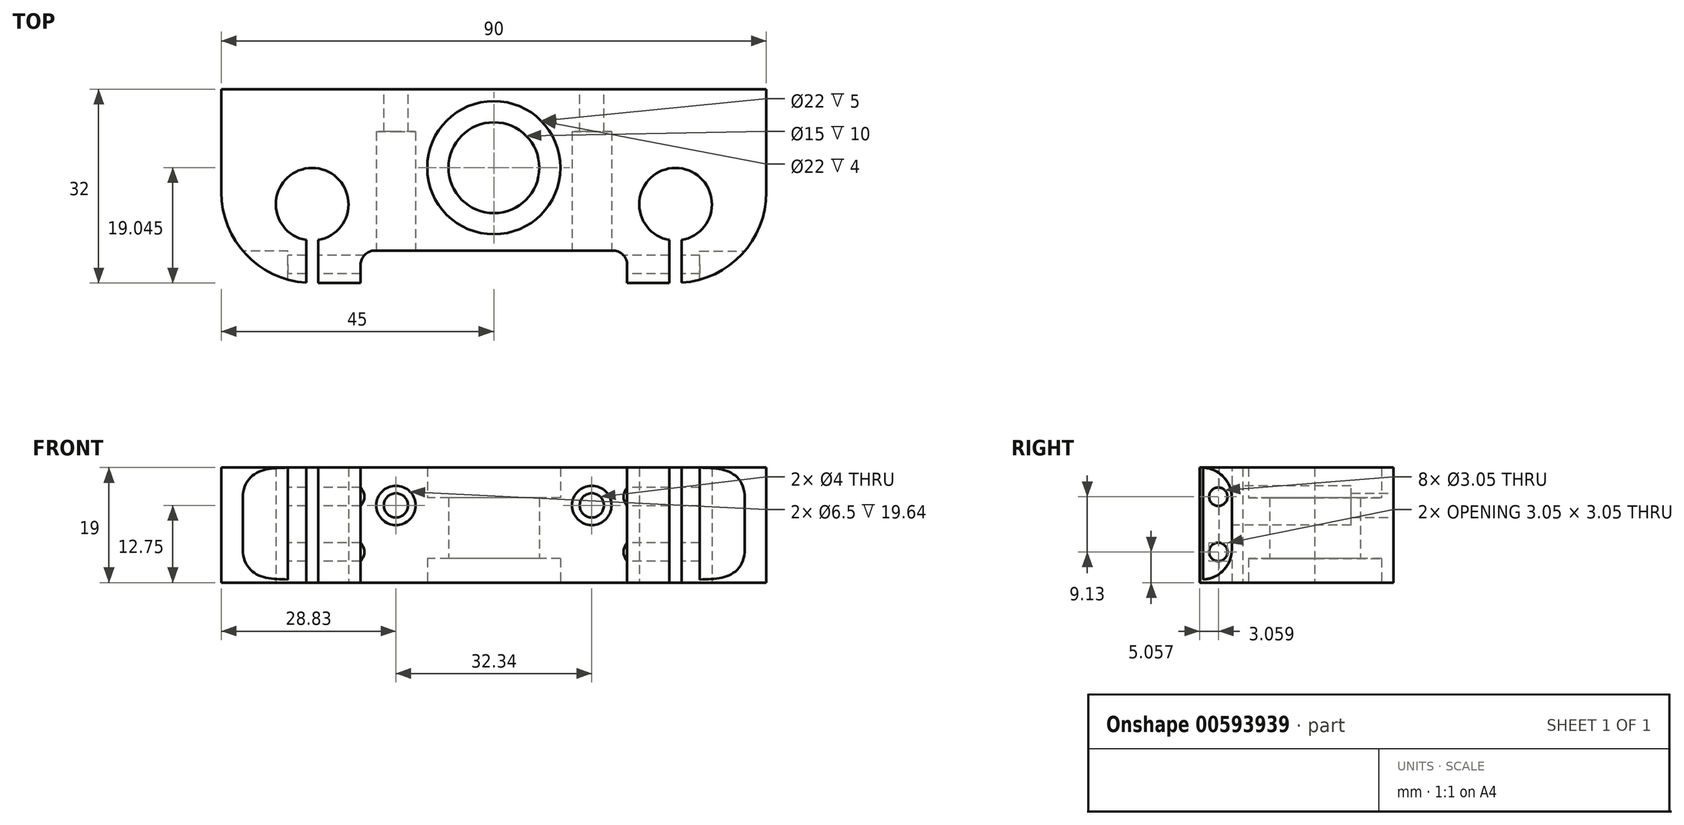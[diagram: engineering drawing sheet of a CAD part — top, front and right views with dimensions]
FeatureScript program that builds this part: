
annotation { "Feature Type Name" : "Feature", "Feature Type Description" : "" }
export const myFeature = defineFeature(function(context is Context, id is Id, definition is map)
    precondition{}
    {
        {
            var Q0;
            Q0=qCreatedBy(makeId("Top.planeOp"),FACE);
            var sketch = newSketch(context, id + "F0", { "sketchPlane" : qUnion([Q0])});
            skLineSegment(sketch, "E0.bottom", {"start": v(0, -8) * mm, "end": v(90, -8) * mm});
            skLineSegment(sketch, "E0.top", {"start": v(15, -40) * mm, "end": v(75, -40) * mm});
            skLineSegment(sketch, "E0.left", {"start": v(0, 0) * mm, "end": v(0, -25) * mm});
            skLineSegment(sketch, "E0.right", {"start": v(90, 0) * mm, "end": v(90, -25) * mm});
            skPoint(sketch, "E1", {"position": v(45, 0) * mm});
            skPoint(sketch, "E2", {"position": v(45, -40) * mm});
            skCircle(sketch, "E3", {"center": v(45, -20.96) * mm, "radius": 11 * mm});
            skCircle(sketch, "E4", {"center": v(45, -20.96) * mm, "radius": 7.5 * mm});
            skCircle(sketch, "E5", {"center": v(15, -27) * mm, "radius": 6 * mm});
            skCircle(sketch, "E6", {"center": v(75, -27) * mm, "radius": 6 * mm});
            skPoint(sketch, "E7.visualSharp", {"position": v(0, -40) * mm});
            skArc(sketch, "E7.filletArc", {"start": v(0, -25) * mm, "mid": v(4.4, -35.6) * mm, "end": v(15, -40) * mm});
            skPoint(sketch, "E8.visualSharp", {"position": v(90, -40) * mm});
            skArc(sketch, "E8.filletArc", {"start": v(75, -40) * mm, "mid": v(85.6, -35.6) * mm, "end": v(90, -25) * mm});
            skLineSegment(sketch, "E9.bottom", {"start": v(16, -40) * mm, "end": v(14, -40) * mm});
            skLineSegment(sketch, "E9.top", {"start": v(16, -14) * mm, "end": v(14, -14) * mm});
            skLineSegment(sketch, "E9.left", {"start": v(16, -40) * mm, "end": v(16, -14) * mm});
            skLineSegment(sketch, "E9.right", {"start": v(14, -40) * mm, "end": v(14, -14) * mm});
            skLineSegment(sketch, "E10.bottom", {"start": v(74, -40) * mm, "end": v(76, -40) * mm});
            skLineSegment(sketch, "E10.top", {"start": v(74, -14) * mm, "end": v(76, -14) * mm});
            skLineSegment(sketch, "E10.left", {"start": v(74, -40) * mm, "end": v(74, -14) * mm});
            skLineSegment(sketch, "E10.right", {"start": v(76, -40) * mm, "end": v(76, -14) * mm});
            skSolve(sketch);
        }
        {
            var Q0;
            Q0=makeQuery(id+"F0.imprint","IMPRINT",FACE,{"disambiguationData":[TD([[makeQuery(id+"F0.imprint","IMPRINT",EDGE,{"derivedFrom":sQuery(id+"F0.wireOp",EDGE,"E0.bottom")}),-1.0]])]});
            var Q1;
            {var subQ5=sQuery(id+"F0.wireOp",EDGE,"E9.top");Q1=makeQuery(id+"F0.imprint","IMPRINT",FACE,{"disambiguationData":[TD([[makeQuery(id+"F0.imprint","IMPRINT",EDGE,{"derivedFrom":subQ5}),1.0]])]});}
            var Q2;
            {var subQ5=sQuery(id+"F0.wireOp",EDGE,"E10.top");Q2=makeQuery(id+"F0.imprint","IMPRINT",FACE,{"disambiguationData":[TD([[makeQuery(id+"F0.imprint","IMPRINT",EDGE,{"derivedFrom":subQ5}),-1.0]])]});}
            extrude(context, id + "F1", {"entities" : qUnion([Q0, Q1, Q2]), "depth" : 25 * mm, "offsetDistance" : 25 * mm});
        }
        {
            var Q0;
            Q0=qCreatedBy(makeId("Right.planeOp"),FACE);
            cPlane(context, id + "F2", {"entities" : qUnion([Q0]), "cplaneType" : CPlaneType.OFFSET, "offset" : 90 * mm, "width" : 150 * mm, "height" : 150 * mm});
        }
        {
            var Q0;
            Q0=qCreatedBy(makeId("Right.planeOp"),FACE);
            var sketch = newSketch(context, id + "F3", { "sketchPlane" : qUnion([Q0])});
            skCircle(sketch, "E11", {"center": v(-36.94, 11.06) * mm, "radius": 1.52 * mm});
            skLineSegment(sketch, "E12.bottom", {"start": v(-39.8, 6.5) * mm, "end": v(-39.7, 6.5) * mm});
            skLineSegment(sketch, "E12.top", {"start": v(-39.8, 25) * mm, "end": v(-39.7, 25) * mm});
            skLineSegment(sketch, "E12.left", {"start": v(-39.8, 6.5) * mm, "end": v(-39.8, 25) * mm});
            skLineSegment(sketch, "E12.right", {"start": v(-34.7, 11.5) * mm, "end": v(-34.7, 20) * mm});
            skPoint(sketch, "E12.middle", {"position": v(-37.25, 15.75) * mm});
            skPoint(sketch, "E13.visualSharp", {"position": v(-34.7, 25) * mm});
            skArc(sketch, "E13.filletArc", {"start": v(-34.7, 20) * mm, "mid": v(-36.16, 23.53) * mm, "end": v(-39.7, 25) * mm});
            skPoint(sketch, "E14.visualSharp", {"position": v(-34.7, 6.5) * mm});
            skArc(sketch, "E14.filletArc", {"start": v(-39.7, 6.5) * mm, "mid": v(-36.16, 7.96) * mm, "end": v(-34.7, 11.5) * mm});
            skCircle(sketch, "E15", {"center": v(-36.94, 20.19) * mm, "radius": 1.52 * mm});
            skSolve(sketch);
        }
        {
            var Q0;
            Q0=makeQuery(id+"F3.imprint","IMPRINT",FACE,{"disambiguationData":[TD([[makeQuery(id+"F3.imprint","IMPRINT",EDGE,{"derivedFrom":sQuery(id+"F3.wireOp",EDGE,"E11")}),1.0]])]});
            var Q1;
            Q1=makeQuery(id+"F3.imprint","IMPRINT",FACE,{"disambiguationData":[TD([[makeQuery(id+"F3.imprint","IMPRINT",EDGE,{"derivedFrom":sQuery(id+"F3.wireOp",EDGE,"E15")}),1.0]])]});
            extrude(context, id + "F4", {"entities" : qUnion([Q0, Q1]), "operationType" : NewBodyOperationType.REMOVE, "depth" : 105.2 * mm, "offsetDistance" : 25 * mm});
        }
        {
            var Q0;
            Q0=makeQuery(id+"F3.imprint","IMPRINT",FACE,{"disambiguationData":[TD([[makeQuery(id+"F3.imprint","IMPRINT",EDGE,{"derivedFrom":sQuery(id+"F3.wireOp",EDGE,"E11")}),-1.0]])]});
            var Q1;
            {var subQ0=sQuery(id+"F3.wireOp",EDGE,"LKILmQxX-aqle-z8wJ-GRMA-pSFsAoVf5IHB.bottom");Q1=makeQuery(id+"F3.imprint","IMPRINT",FACE,{"disambiguationData":[TD([[makeQuery(id+"F3.imprint","IMPRINT",EDGE,{"derivedFrom":subQ0}),1.0]])]});}
            extrude(context, id + "F5", {"entities" : qUnion([Q0, Q1]), "operationType" : NewBodyOperationType.REMOVE, "depth" : 11 * mm, "offsetDistance" : 25 * mm});
        }
        {
            var Q0;
            Q0=qCreatedBy(id+"F2.planeOp",FACE);
            var sketch = newSketch(context, id + "F6", { "sketchPlane" : qUnion([Q0])});
            skCircle(sketch, "E16", {"center": v(-112.54, 53.34) * mm, "radius": 1.52 * mm});
            skLineSegment(sketch, "E17.bottom", {"start": v(-39.8, 6.5) * mm, "end": v(-39.7, 6.5) * mm});
            skLineSegment(sketch, "E17.top", {"start": v(-39.8, 25) * mm, "end": v(-39.7, 25) * mm});
            skLineSegment(sketch, "E17.left", {"start": v(-39.8, 6.5) * mm, "end": v(-39.8, 25) * mm});
            skLineSegment(sketch, "E17.right", {"start": v(-34.7, 11.5) * mm, "end": v(-34.7, 20) * mm});
            skPoint(sketch, "E17.middle", {"position": v(-37.25, 15.75) * mm});
            skPoint(sketch, "E18.visualSharp", {"position": v(-34.7, 25) * mm});
            skArc(sketch, "E18.filletArc", {"start": v(-34.7, 20) * mm, "mid": v(-36.16, 23.53) * mm, "end": v(-39.7, 25) * mm});
            skPoint(sketch, "E19.visualSharp", {"position": v(-34.7, 6.5) * mm});
            skArc(sketch, "E19.filletArc", {"start": v(-39.7, 6.5) * mm, "mid": v(-36.16, 7.96) * mm, "end": v(-34.7, 11.5) * mm});
            skCircle(sketch, "E20", {"center": v(-112.54, 62.47) * mm, "radius": 1.52 * mm});
            skSolve(sketch);
        }
        {
            var Q0;
            Q0=makeQuery(id+"F6.imprint","IMPRINT",FACE,{"disambiguationData":[TD([[makeQuery(id+"F6.imprint","IMPRINT",EDGE,{"derivedFrom":sQuery(id+"F6.wireOp",EDGE,"E17.bottom")}),1.0]])]});
            extrude(context, id + "F7", {"entities" : qUnion([Q0]), "operationType" : NewBodyOperationType.REMOVE, "oppositeDirection" : true, "depth" : 11 * mm, "offsetDistance" : 25 * mm});
        }
        {
            var Q0;
            Q0=makeQuery(id+"F0.imprint","IMPRINT",FACE,{"disambiguationData":[TD([[makeQuery(id+"F0.imprint","IMPRINT",EDGE,{"derivedFrom":sQuery(id+"F0.wireOp",EDGE,"E3")}),1.0]])]});
            extrude(context, id + "F8", {"entities" : qUnion([Q0]), "operationType" : NewBodyOperationType.ADD, "depth" : 20 * mm, "offsetDistance" : 25 * mm});
        }
        {
            var Q0;
            Q0=makeQuery(id+"F0.imprint","IMPRINT",FACE,{"disambiguationData":[TD([[makeQuery(id+"F0.imprint","IMPRINT",EDGE,{"derivedFrom":sQuery(id+"F0.wireOp",EDGE,"E3")}),1.0]])]});
            extrude(context, id + "F9", {"entities" : qUnion([Q0]), "operationType" : NewBodyOperationType.REMOVE, "depth" : 5 * mm, "offsetDistance" : 25 * mm});
        }
        {
            var Q0;
            Q0=makeQuery(id+"F1.opExtrude","SWEPT_FACE",FACE,{"disambiguationData":[OSD([sQuery(id+"F0.wireOp",EDGE,"E0.bottom")])]});
            var sketch = newSketch(context, id + "F10", { "sketchPlane" : qUnion([Q0])});
            skCircle(sketch, "E21", {"center": v(-45, 18.75) * mm, "radius": 2 * mm});
            skPoint(sketch, "E21.centerSnap0", {"position": v(-45, 25) * mm});
            skPoint(sketch, "E21.centerSnap1", {"position": v(0, 12.5) * mm});
            skCircle(sketch, "E22.1.0.0", {"center": v(-28.83, 18.75) * mm, "radius": 2 * mm});
            skLineSegment(sketch, "E22.direction1", {"start": v(-45, 18.75) * mm, "end": v(-28.83, 18.75) * mm, "construction": true});
            skCircle(sketch, "E23.1.0.0", {"center": v(-61.17, 18.75) * mm, "radius": 2 * mm});
            skLineSegment(sketch, "E23.direction1", {"start": v(-45, 18.75) * mm, "end": v(-61.17, 18.75) * mm, "construction": true});
            skPoint(sketch, "E24", {"position": v(0, 25) * mm});
            skLineSegment(sketch, "E25.direction1", {"start": v(-28.83, 18.75) * mm, "end": v(-28.83, 18.75) * mm});
            skLineSegment(sketch, "E25.direction2", {"start": v(-28.83, 18.75) * mm, "end": v(-28.78, 6.25) * mm, "construction": true});
            skSolve(sketch);
        }
        {
            var Q0;
            Q0=makeQuery(id+"F10.imprint","IMPRINT",FACE,{"disambiguationData":[TD([[makeQuery(id+"F10.imprint","IMPRINT",EDGE,{"derivedFrom":sQuery(id+"F10.wireOp",EDGE,"E25.2.0.2")}),1.0]])]});
            var Q1;
            Q1=makeQuery(id+"F10.imprint","IMPRINT",FACE,{"disambiguationData":[TD([[makeQuery(id+"F10.imprint","IMPRINT",EDGE,{"derivedFrom":sQuery(id+"F10.wireOp",EDGE,"E22.1.0.0")}),1.0]])]});
            var Q2;
            Q2=makeQuery(id+"F10.imprint","IMPRINT",FACE,{"disambiguationData":[TD([[makeQuery(id+"F10.imprint","IMPRINT",EDGE,{"derivedFrom":sQuery(id+"F10.wireOp",EDGE,"E25.2.1.2")}),1.0]])]});
            var Q3;
            Q3=makeQuery(id+"F10.imprint","IMPRINT",FACE,{"disambiguationData":[TD([[makeQuery(id+"F10.imprint","IMPRINT",EDGE,{"derivedFrom":sQuery(id+"F10.wireOp",EDGE,"E25.2.1.0")}),1.0]])]});
            var Q4;
            Q4=makeQuery(id+"F10.imprint","IMPRINT",FACE,{"disambiguationData":[TD([[makeQuery(id+"F10.imprint","IMPRINT",EDGE,{"derivedFrom":sQuery(id+"F10.wireOp",EDGE,"E23.1.0.0")}),1.0]])]});
            extrude(context, id + "F11", {"entities" : qUnion([Q0, Q1, Q2, Q3, Q4]), "operationType" : NewBodyOperationType.REMOVE, "oppositeDirection" : true, "depth" : 10 * mm, "offsetDistance" : 25 * mm});
        }
        {
            var Q0;
            Q0=makeQuery(id+"F1.opExtrude","CAP_FACE",FACE,{"disambiguationData":[OSD([sQuery(id+"F0.wireOp",EDGE,"E0.bottom"),sQuery(id+"F0.wireOp",EDGE,"E0.top"),sQuery(id+"F0.wireOp",EDGE,"E0.left"),sQuery(id+"F0.wireOp",EDGE,"E0.right"),sQuery(id+"F0.wireOp",EDGE,"E3"),sQuery(id+"F0.wireOp",EDGE,"E5"),sQuery(id+"F0.wireOp",EDGE,"E6"),sQuery(id+"F0.wireOp",EDGE,"E7.filletArc"),sQuery(id+"F0.wireOp",EDGE,"E8.filletArc"),sQuery(id+"F0.wireOp",EDGE,"E9.left"),sQuery(id+"F0.wireOp",EDGE,"E9.right"),sQuery(id+"F0.wireOp",EDGE,"E10.left"),sQuery(id+"F0.wireOp",EDGE,"E10.right")])],"isStart":false});
            var sketch = newSketch(context, id + "F12", { "sketchPlane" : qUnion([Q0])});
            skLineSegment(sketch, "E26.bottom", {"start": v(64.62, -34.64) * mm, "end": v(25.39, -34.64) * mm});
            skPoint(sketch, "E26.middle", {"position": v(45, -40) * mm});
            skLineSegment(sketch, "E27", {"start": v(45, -8) * mm, "end": v(45, -40) * mm});
            skPoint(sketch, "E28.visualSharp", {"position": v(28.32, -34.64) * mm});
            skArc(sketch, "E28.filletArc", {"start": v(25.39, -34.64) * mm, "mid": v(23.7, -35.34) * mm, "end": v(23, -37.03) * mm});
            skPoint(sketch, "E29.visualSharp", {"position": v(59.63, -34.64) * mm});
            skArc(sketch, "E29.filletArc", {"start": v(67, -36.79) * mm, "mid": v(66.23, -35.26) * mm, "end": v(64.62, -34.64) * mm});
            skPoint(sketch, "E30", {"position": v(23, -40) * mm});
            skPoint(sketch, "E31", {"position": v(67, -40) * mm});
            skLineSegment(sketch, "E32", {"start": v(23, -37.03) * mm, "end": v(23, -40) * mm});
            skLineSegment(sketch, "E33", {"start": v(67, -36.79) * mm, "end": v(67, -40) * mm});
            skSolve(sketch);
        }
        {
            var Q0;
            {var subQ5=sQuery(id+"F12.wireOp",EDGE,"E28.filletArc");Q0=makeQuery(id+"F12.imprint","IMPRINT",FACE,{"disambiguationData":[TD([[makeQuery(id+"F12.imprint","IMPRINT",EDGE,{"derivedFrom":subQ5}),1.0]])]});}
            var Q1;
            {var subQ0=sQuery(id+"F12.wireOp",EDGE,"E29.filletArc");Q1=makeQuery(id+"F12.imprint","IMPRINT",FACE,{"disambiguationData":[TD([[makeQuery(id+"F12.imprint","IMPRINT",EDGE,{"derivedFrom":subQ0}),1.0]])]});}
            extrude(context, id + "F13", {"entities" : qUnion([Q0, Q1]), "operationType" : NewBodyOperationType.REMOVE, "endBound" : BoundingType.THROUGH_ALL, "oppositeDirection" : true, "depth" : 25 * mm, "offsetDistance" : 25 * mm});
        }
        {
            var Q0;
            {var subQ13=sQuery(id+"F0.wireOp",EDGE,"E0.bottom");Q0=makeQuery(id+"F0.imprint","IMPRINT",FACE,{"disambiguationData":[TD([[makeQuery(id+"F0.imprint","IMPRINT",EDGE,{"derivedFrom":subQ13}),-1.0]])]});}
            var Q1;
            {var subQ5=sQuery(id+"F0.wireOp",EDGE,"E9.top");Q1=makeQuery(id+"F0.imprint","IMPRINT",FACE,{"disambiguationData":[TD([[makeQuery(id+"F0.imprint","IMPRINT",EDGE,{"derivedFrom":subQ5}),1.0]])]});}
            var Q2;
            {var subQ5=sQuery(id+"F0.wireOp",EDGE,"E10.top");Q2=makeQuery(id+"F0.imprint","IMPRINT",FACE,{"disambiguationData":[TD([[makeQuery(id+"F0.imprint","IMPRINT",EDGE,{"derivedFrom":subQ5}),-1.0]])]});}
            var Q3;
            Q3=makeQuery(id+"F0.imprint","IMPRINT",FACE,{"disambiguationData":[TD([[makeQuery(id+"F0.imprint","IMPRINT",EDGE,{"derivedFrom":sQuery(id+"F0.wireOp",EDGE,"E3")}),1.0]])]});
            extrude(context, id + "F14", {"entities" : qUnion([Q0, Q1, Q2, Q3]), "operationType" : NewBodyOperationType.REMOVE, "oppositeDirection" : true, "depth" : -6 * mm, "offsetDistance" : 25 * mm});
        }
        {
            var Q0;
            Q0=makeQuery(id+"F0.imprint","IMPRINT",FACE,{"disambiguationData":[TD([[makeQuery(id+"F0.imprint","IMPRINT",EDGE,{"derivedFrom":sQuery(id+"F0.wireOp",EDGE,"E3")}),1.0]])]});
            extrude(context, id + "F15", {"entities" : qUnion([Q0]), "operationType" : NewBodyOperationType.REMOVE, "depth" : 10 * mm, "offsetDistance" : 25 * mm});
        }
        {
            var Q0;
            {var subQ1=sQuery(id+"F0.wireOp",EDGE,"E10.left");var subQ11=sQuery(id+"F0.wireOp",EDGE,"E0.top");Q0=makeQuery(id+"F13.boolean.opBoolean","SPLIT",FACE,{"disambiguationData":[TD([makeQuery(id+"F1.opExtrude","SWEPT_FACE",FACE,{"disambiguationData":[OSD([subQ1])]})])],"derivedFrom":makeQuery(id+"F1.opExtrude","SWEPT_FACE",FACE,{"disambiguationData":[OSD([subQ11])]})});}
            var sketch = newSketch(context, id + "F16", { "sketchPlane" : qUnion([Q0])});
            skCircle(sketch, "E34", {"center": v(45, 18.75) * mm, "radius": 3.25 * mm});
            skPoint(sketch, "E34.centerSnap0", {"position": v(45, 25) * mm});
            skPoint(sketch, "E34.centerSnap1", {"position": v(89.33, 8.73) * mm});
            skCircle(sketch, "E35.1.0.0", {"center": v(61.17, 18.75) * mm, "radius": 3.25 * mm});
            skLineSegment(sketch, "E35.direction1", {"start": v(45, 18.75) * mm, "end": v(61.17, 18.75) * mm, "construction": true});
            skCircle(sketch, "E36.1.0.0", {"center": v(28.83, 18.75) * mm, "radius": 3.25 * mm});
            skLineSegment(sketch, "E36.direction1", {"start": v(45, 18.75) * mm, "end": v(28.83, 18.75) * mm, "construction": true});
            skPoint(sketch, "E37", {"position": v(89.33, 21.23) * mm});
            skLineSegment(sketch, "E38.direction1", {"start": v(140.1, 62.28) * mm, "end": v(140.1, 62.28) * mm});
            skSolve(sketch);
        }
        {
            var Q0;
            Q0=makeQuery(id+"F16.imprint","IMPRINT",FACE,{"disambiguationData":[TD([[makeQuery(id+"F16.imprint","IMPRINT",EDGE,{"derivedFrom":sQuery(id+"F16.wireOp",EDGE,"E36.1.0.0")}),1.0]])]});
            var Q1;
            Q1=makeQuery(id+"F16.imprint","IMPRINT",FACE,{"disambiguationData":[TD([[makeQuery(id+"F16.imprint","IMPRINT",EDGE,{"derivedFrom":sQuery(id+"F16.wireOp",EDGE,"E35.1.0.0")}),1.0]])]});
            extrude(context, id + "F17", {"entities" : qUnion([Q0, Q1]), "operationType" : NewBodyOperationType.REMOVE, "oppositeDirection" : true, "depth" : 25 * mm, "offsetDistance" : 25 * mm});
        }
    });
